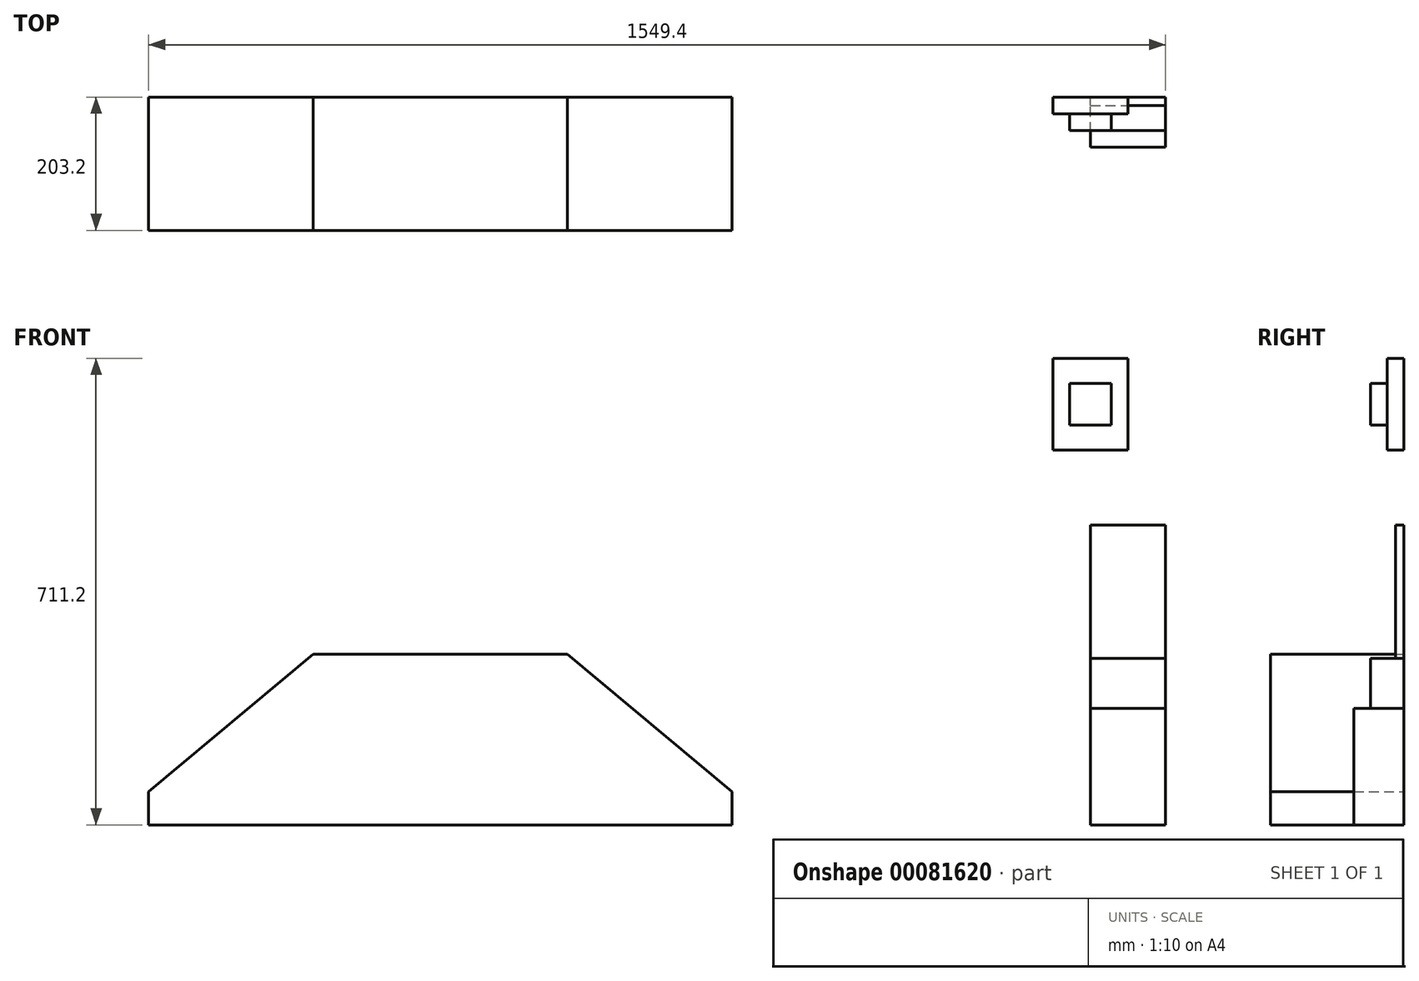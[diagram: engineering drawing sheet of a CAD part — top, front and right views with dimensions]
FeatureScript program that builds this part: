
annotation { "Feature Type Name" : "Feature", "Feature Type Description" : "" }
export const myFeature = defineFeature(function(context is Context, id is Id, definition is map)
    precondition{}
    {
        {
            var Q0;
            Q0=qCreatedBy(makeId("Front.planeOp"),FACE);
            var sketch = newSketch(context, id + "F0", { "sketchPlane" : qUnion([Q0])});
            skLineSegment(sketch, "E0", {"start": v(0, 0) * mm, "end": v(546.1, 0) * mm, "construction": true});
            skLineSegment(sketch, "E1", {"start": v(546.1, 0) * mm, "end": v(660.4, 0) * mm, "construction": true});
            skLineSegment(sketch, "E2", {"start": v(660.4, 0) * mm, "end": v(2006.6, 0) * mm, "construction": true});
            skLineSegment(sketch, "E3", {"start": v(-800.1, 552.45) * mm, "end": v(2006.6, 552.45) * mm, "construction": true});
            skLineSegment(sketch, "E4", {"start": v(-800.1, 488.95) * mm, "end": v(2006.6, 488.95) * mm, "construction": true});
            skLineSegment(sketch, "E5", {"start": v(546.1, 0) * mm, "end": v(546.1, 254) * mm, "construction": true});
            skLineSegment(sketch, "E6", {"start": v(546.1, 457.2) * mm, "end": v(660.4, 457.2) * mm, "construction": true});
            skLineSegment(sketch, "E7", {"start": v(660.4, 457.2) * mm, "end": v(660.4, 0) * mm, "construction": true});
            skLineSegment(sketch, "E8", {"start": v(546.1, 254) * mm, "end": v(546.1, 457.2) * mm, "construction": true});
            skLineSegment(sketch, "E9", {"start": v(546.1, 254) * mm, "end": v(660.4, 254) * mm, "construction": true});
            skLineSegment(sketch, "E10", {"start": v(0, 0) * mm, "end": v(-250.83, 0) * mm});
            skLineSegment(sketch, "E11", {"start": v(-1219.2, 0) * mm, "end": v(-1219.2, 1165.4) * mm, "construction": true});
            skLineSegment(sketch, "E12.left", {"start": v(2006.6, 0) * mm, "end": v(2006.6, 1152.5) * mm, "construction": true});
            skLineSegment(sketch, "E12.right", {"start": v(1447.8, 0) * mm, "end": v(1447.8, 1156.25) * mm, "construction": true});
            skLineSegment(sketch, "E13", {"start": v(-889, 0) * mm, "end": v(-1219.2, 0) * mm, "construction": true});
            skLineSegment(sketch, "E14", {"start": v(-889, 0) * mm, "end": v(-889, 50.8) * mm});
            skLineSegment(sketch, "E15", {"start": v(-889, 50.8) * mm, "end": v(-638.18, 260.35) * mm});
            skLineSegment(sketch, "E16", {"start": v(-250.83, 260.35) * mm, "end": v(0, 50.8) * mm});
            skLineSegment(sketch, "E17", {"start": v(0, 50.8) * mm, "end": v(0, 0) * mm, "construction": true});
            skLineSegment(sketch, "E18", {"start": v(-638.18, 260.35) * mm, "end": v(-250.83, 260.35) * mm});
            skLineSegment(sketch, "E19", {"start": v(-250.83, 260.35) * mm, "end": v(-250.83, 0) * mm, "construction": true});
            skLineSegment(sketch, "E20", {"start": v(-638.18, 260.35) * mm, "end": v(-638.18, 0) * mm, "construction": true});
            skLineSegment(sketch, "E21", {"start": v(546.1, 177.8) * mm, "end": v(660.4, 177.8) * mm, "construction": true});
            skLineSegment(sketch, "E22.bottom", {"start": v(577.85, 673.1) * mm, "end": v(514.35, 673.1) * mm, "construction": true});
            skLineSegment(sketch, "E22.top", {"start": v(577.85, 609.6) * mm, "end": v(514.35, 609.6) * mm, "construction": true});
            skLineSegment(sketch, "E22.left", {"start": v(577.85, 673.1) * mm, "end": v(577.85, 609.6) * mm, "construction": true});
            skLineSegment(sketch, "E22.right", {"start": v(514.35, 673.1) * mm, "end": v(514.35, 609.6) * mm, "construction": true});
            skPoint(sketch, "E22.middle", {"position": v(546.1, 641.35) * mm});
            skLineSegment(sketch, "E23.bottom", {"start": v(603.25, 711.2) * mm, "end": v(488.95, 711.2) * mm, "construction": true});
            skLineSegment(sketch, "E23.top", {"start": v(603.25, 571.5) * mm, "end": v(488.95, 571.5) * mm, "construction": true});
            skLineSegment(sketch, "E23.left", {"start": v(603.25, 711.2) * mm, "end": v(603.25, 571.5) * mm, "construction": true});
            skLineSegment(sketch, "E23.right", {"start": v(488.95, 711.2) * mm, "end": v(488.95, 571.5) * mm, "construction": true});
            skLineSegment(sketch, "E24", {"start": v(-889, 0) * mm, "end": v(-1398.29, 0) * mm, "construction": true});
            skLineSegment(sketch, "E25", {"start": v(-638.18, 0) * mm, "end": v(-889, 0) * mm});
            skLineSegment(sketch, "E26", {"start": v(-250.83, 0) * mm, "end": v(-638.18, 0) * mm});
            skSolve(sketch);
        }
        {
            var Q0;
            Q0=qCreatedBy(makeId("Front.planeOp"),FACE);
            var sketch = newSketch(context, id + "F1", { "sketchPlane" : qUnion([Q0])});
            skLineSegment(sketch, "E27", {"start": v(0, 0) * mm, "end": v(546.1, 0) * mm, "construction": true});
            skLineSegment(sketch, "E28", {"start": v(546.1, 0) * mm, "end": v(660.4, 0) * mm});
            skLineSegment(sketch, "E29", {"start": v(660.4, 0) * mm, "end": v(2006.6, 0) * mm, "construction": true});
            skLineSegment(sketch, "E30", {"start": v(-800.1, 552.45) * mm, "end": v(2006.6, 552.45) * mm, "construction": true});
            skLineSegment(sketch, "E31", {"start": v(-800.1, 488.95) * mm, "end": v(2006.6, 488.95) * mm, "construction": true});
            skLineSegment(sketch, "E32", {"start": v(546.1, 0) * mm, "end": v(546.1, 177.8) * mm});
            skLineSegment(sketch, "E33", {"start": v(546.1, 457.2) * mm, "end": v(660.4, 457.2) * mm});
            skLineSegment(sketch, "E34", {"start": v(660.4, 457.2) * mm, "end": v(660.4, 254) * mm});
            skLineSegment(sketch, "E35", {"start": v(546.1, 254) * mm, "end": v(546.1, 457.2) * mm});
            skLineSegment(sketch, "E36", {"start": v(546.1, 254) * mm, "end": v(660.4, 254) * mm});
            skLineSegment(sketch, "E37", {"start": v(0, 0) * mm, "end": v(-250.83, 0) * mm});
            skLineSegment(sketch, "E38", {"start": v(-1219.2, 0) * mm, "end": v(-1219.2, 1227.6) * mm, "construction": true});
            skLineSegment(sketch, "E39.left", {"start": v(2006.6, 0) * mm, "end": v(2006.6, 1214.69) * mm, "construction": true});
            skLineSegment(sketch, "E39.right", {"start": v(1447.8, 0) * mm, "end": v(1447.8, 1218.45) * mm, "construction": true});
            skLineSegment(sketch, "E40", {"start": v(-889, 0) * mm, "end": v(-1219.2, 0) * mm, "construction": true});
            skLineSegment(sketch, "E41", {"start": v(-889, 0) * mm, "end": v(-889, 50.8) * mm});
            skLineSegment(sketch, "E42", {"start": v(-889, 50.8) * mm, "end": v(-638.17, 260.35) * mm});
            skLineSegment(sketch, "E43", {"start": v(-250.83, 260.35) * mm, "end": v(0, 50.8) * mm});
            skLineSegment(sketch, "E44", {"start": v(0, 50.8) * mm, "end": v(0, 0) * mm});
            skLineSegment(sketch, "E45", {"start": v(-638.18, 260.35) * mm, "end": v(-250.83, 260.35) * mm});
            skLineSegment(sketch, "E46", {"start": v(-250.83, 260.35) * mm, "end": v(-250.83, 0) * mm, "construction": true});
            skLineSegment(sketch, "E47", {"start": v(-638.18, 260.35) * mm, "end": v(-638.18, 0) * mm, "construction": true});
            skLineSegment(sketch, "E48", {"start": v(546.1, 177.8) * mm, "end": v(546.1, 177.8) * mm});
            skLineSegment(sketch, "E49.bottom", {"start": v(577.85, 673.1) * mm, "end": v(514.35, 673.1) * mm});
            skLineSegment(sketch, "E49.top", {"start": v(577.85, 609.6) * mm, "end": v(514.35, 609.6) * mm});
            skLineSegment(sketch, "E49.left", {"start": v(577.85, 673.1) * mm, "end": v(577.85, 609.6) * mm});
            skLineSegment(sketch, "E49.right", {"start": v(514.35, 673.1) * mm, "end": v(514.35, 609.6) * mm});
            skPoint(sketch, "E49.middle", {"position": v(546.1, 641.35) * mm});
            skLineSegment(sketch, "E50.bottom", {"start": v(603.25, 711.2) * mm, "end": v(488.95, 711.2) * mm});
            skLineSegment(sketch, "E50.top", {"start": v(603.25, 571.5) * mm, "end": v(488.95, 571.5) * mm});
            skLineSegment(sketch, "E50.left", {"start": v(603.25, 711.2) * mm, "end": v(603.25, 571.5) * mm});
            skLineSegment(sketch, "E50.right", {"start": v(488.95, 711.2) * mm, "end": v(488.95, 571.5) * mm});
            skLineSegment(sketch, "E51", {"start": v(-889, 0) * mm, "end": v(-1703.4, 0) * mm, "construction": true});
            skLineSegment(sketch, "E52", {"start": v(546.1, 177.8) * mm, "end": v(660.4, 177.8) * mm});
            skLineSegment(sketch, "E53", {"start": v(546.1, 177.8) * mm, "end": v(546.1, 254) * mm});
            skLineSegment(sketch, "E54", {"start": v(660.4, 177.8) * mm, "end": v(660.4, 0) * mm});
            skLineSegment(sketch, "E55", {"start": v(660.4, 254) * mm, "end": v(660.4, 177.8) * mm});
            skLineSegment(sketch, "E56", {"start": v(-638.18, 0) * mm, "end": v(-889, 0) * mm});
            skLineSegment(sketch, "E57", {"start": v(-250.83, 0) * mm, "end": v(-250.83, 0) * mm});
            skLineSegment(sketch, "E58", {"start": v(-250.83, 0) * mm, "end": v(-638.18, 0) * mm});
            skSolve(sketch);
        }
        {
            var Q0;
            Q0=makeQuery(id+"F1.imprint","IMPRINT",FACE,{"disambiguationData":[TD([[makeQuery(id+"F1.imprint","IMPRINT",EDGE,{"derivedFrom":sQuery(id+"F1.wireOp",EDGE,"E37")}),-1.0]])]});
            extrude(context, id + "F2", {"entities" : qUnion([Q0]), "depth" : 203.2 * mm});
        }
        {
            var Q0;
            Q0=makeQuery(id+"F1.imprint","IMPRINT",FACE,{"disambiguationData":[TD([[makeQuery(id+"F1.imprint","IMPRINT",EDGE,{"derivedFrom":sQuery(id+"F1.wireOp",EDGE,"E28")}),1.0]])]});
            extrude(context, id + "F3", {"entities" : qUnion([Q0]), "depth" : 76.2 * mm});
        }
        {
            var Q0;
            Q0=makeQuery(id+"F1.imprint","IMPRINT",FACE,{"disambiguationData":[TD([[makeQuery(id+"F1.imprint","IMPRINT",EDGE,{"derivedFrom":sQuery(id+"F1.wireOp",EDGE,"E33")}),-1.0]])]});
            extrude(context, id + "F4", {"entities" : qUnion([Q0]), "depth" : 12.7 * mm});
        }
        {
            var Q0;
            Q0=makeQuery(id+"F1.imprint","IMPRINT",FACE,{"disambiguationData":[TD([[makeQuery(id+"F1.imprint","IMPRINT",EDGE,{"derivedFrom":sQuery(id+"F1.wireOp",EDGE,"E36")}),-1.0]])]});
            extrude(context, id + "F5", {"entities" : qUnion([Q0]), "depth" : 50.8 * mm});
        }
        {
            var Q0;
            Q0=makeQuery(id+"F1.imprint","IMPRINT",FACE,{"disambiguationData":[TD([[makeQuery(id+"F1.imprint","IMPRINT",EDGE,{"derivedFrom":sQuery(id+"F1.wireOp",EDGE,"E49.bottom")}),-1.0]])]});
            extrude(context, id + "F6", {"entities" : qUnion([Q0]), "depth" : 25.4 * mm});
        }
        {
            var Q0;
            Q0=makeQuery(id+"F1.imprint","IMPRINT",FACE,{"disambiguationData":[TD([[makeQuery(id+"F1.imprint","IMPRINT",EDGE,{"derivedFrom":sQuery(id+"F1.wireOp",EDGE,"E49.bottom")}),1.0]])]});
            extrude(context, id + "F7", {"entities" : qUnion([Q0]), "operationType" : NewBodyOperationType.ADD, "depth" : 50.8 * mm});
        }
    });
